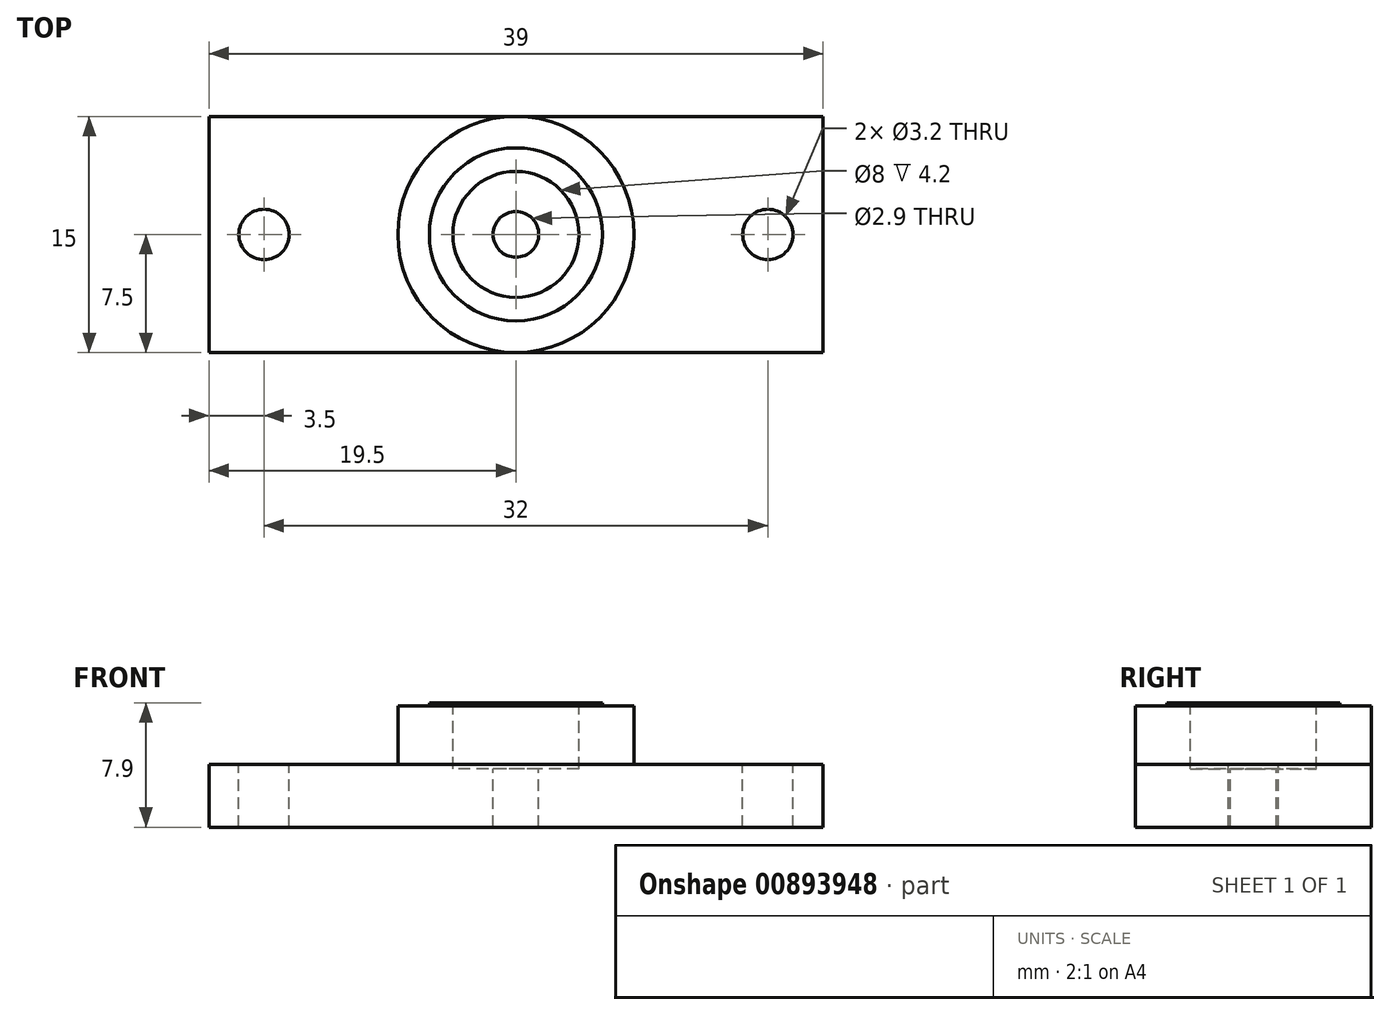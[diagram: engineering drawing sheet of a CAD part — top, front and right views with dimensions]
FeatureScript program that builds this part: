
annotation { "Feature Type Name" : "Feature", "Feature Type Description" : "" }
export const myFeature = defineFeature(function(context is Context, id is Id, definition is map)
    precondition{}
    {
        {
            var Q0;
            Q0=qCreatedBy(makeId("Top.planeOp"),FACE);
            var sketch = newSketch(context, id + "F0", { "sketchPlane" : qUnion([Q0])});
            skLineSegment(sketch, "E0.bottom", {"start": v(0, 0) * mm, "end": v(39, 0) * mm});
            skLineSegment(sketch, "E0.top", {"start": v(0, 15) * mm, "end": v(39, 15) * mm});
            skLineSegment(sketch, "E0.left", {"start": v(0, 0) * mm, "end": v(0, 15) * mm});
            skLineSegment(sketch, "E0.right", {"start": v(39, 0) * mm, "end": v(39, 15) * mm});
            skSolve(sketch);
        }
        {
            var Q0;
            Q0 = qSketchRegion(id + "F0", true);
            extrude(context, id + "F1", {"entities" : qUnion([Q0]), "depth" : 4 * mm, "offsetDistance" : 25 * mm});
        }
        {
            var Q0;
            Q0=makeQuery(id+"F1.opExtrude","CAP_FACE",FACE,{"disambiguationData":[OSD([sQuery(id+"F0.wireOp",EDGE,"E0.bottom"),sQuery(id+"F0.wireOp",EDGE,"E0.top"),sQuery(id+"F0.wireOp",EDGE,"E0.left"),sQuery(id+"F0.wireOp",EDGE,"E0.right")])],"isStart":false});
            var sketch = newSketch(context, id + "F2", { "sketchPlane" : qUnion([Q0])});
            skLineSegment(sketch, "E1", {"start": v(0, 7.5) * mm, "end": v(39, 7.5) * mm, "construction": true});
            skLineSegment(sketch, "E2", {"start": v(19.5, 15) * mm, "end": v(19.5, 0) * mm, "construction": true});
            skCircle(sketch, "E3", {"center": v(19.5, 7.5) * mm, "radius": 7.5 * mm});
            skSolve(sketch);
        }
        {
            var Q0;
            Q0 = qSketchRegion(id + "F2", true);
            extrude(context, id + "F3", {"entities" : qUnion([Q0]), "operationType" : NewBodyOperationType.ADD, "depth" : 3.9 * mm, "offsetDistance" : 25 * mm});
        }
        {
            var Q0;
            Q0=makeQuery(id+"F3.opExtrude","CAP_FACE",FACE,{"disambiguationData":[OSD([sQuery(id+"F2.wireOp",EDGE,"E3")])],"isStart":false});
            var sketch = newSketch(context, id + "F4", { "sketchPlane" : qUnion([Q0])});
            skCircle(sketch, "E4", {"center": v(19.5, 7.5) * mm, "radius": 4 * mm});
            skLineSegment(sketch, "E5", {"start": v(19.5, 15) * mm, "end": v(19.5, 0) * mm, "construction": true});
            skLineSegment(sketch, "E6", {"start": v(12, 7.5) * mm, "end": v(27, 7.5) * mm, "construction": true});
            skSolve(sketch);
        }
        {
            var Q0;
            Q0 = qSketchRegion(id + "F4", true);
            extrude(context, id + "F5", {"entities" : qUnion([Q0]), "operationType" : NewBodyOperationType.REMOVE, "depth" : -4.2 * mm, "offsetDistance" : 25 * mm});
        }
        {
            var Q0;
            Q0=makeQuery(id+"F1.opExtrude","CAP_FACE",FACE,{"disambiguationData":[OSD([sQuery(id+"F0.wireOp",EDGE,"E0.bottom"),sQuery(id+"F0.wireOp",EDGE,"E0.top"),sQuery(id+"F0.wireOp",EDGE,"E0.left"),sQuery(id+"F0.wireOp",EDGE,"E0.right")])],"isStart":false});
            var sketch = newSketch(context, id + "F6", { "sketchPlane" : qUnion([Q0])});
            skLineSegment(sketch, "E7", {"start": v(39, 7.5) * mm, "end": v(0, 7.5) * mm, "construction": true});
            skLineSegment(sketch, "E8", {"start": v(35.5, 15) * mm, "end": v(35.5, 0) * mm, "construction": true});
            skCircle(sketch, "E9.MirrorC", {"center": v(35.5, 7.5) * mm, "radius": 1.6 * mm});
            skCircle(sketch, "E10.MirrorC", {"center": v(3.5, 7.5) * mm, "radius": 1.6 * mm});
            skSolve(sketch);
        }
        {
            var Q0;
            Q0 = qSketchRegion(id + "F6", true);
            var Q1;
            Q1=makeQuery(id+"F6.imprint","IMPRINT",FACE,{"disambiguationData":[TD([[makeQuery(id+"F6.imprint","IMPRINT",EDGE,{"derivedFrom":sQuery(id+"F6.wireOp",EDGE,"maGDqfsK-tZUu-O8Bw-q2Sx-ifdf9yk7xXRb")}),1.0]])]});
            extrude(context, id + "F7", {"entities" : qUnion([Q0, Q1]), "operationType" : NewBodyOperationType.REMOVE, "oppositeDirection" : true, "depth" : 25 * mm, "offsetDistance" : 25 * mm});
        }
        {
            var Q0;
            Q0=makeQuery(id+"F5.boolean.opBoolean","COPY",FACE,{"derivedFrom":makeQuery(id+"F5.opExtrude","CAP_FACE",FACE,{"disambiguationData":[OSD([sQuery(id+"F4.wireOp",EDGE,"E4")])],"isStart":false})});
            var sketch = newSketch(context, id + "F8", { "sketchPlane" : qUnion([Q0])});
            skLineSegment(sketch, "E11", {"start": v(19.5, 11.5) * mm, "end": v(19.5, 3.5) * mm, "construction": true});
            skLineSegment(sketch, "E12", {"start": v(15.5, 7.5) * mm, "end": v(23.5, 7.5) * mm, "construction": true});
            skCircle(sketch, "E13", {"center": v(19.5, 7.5) * mm, "radius": 1.45 * mm});
            skSolve(sketch);
        }
        {
            var Q0;
            Q0 = qSketchRegion(id + "F8", true);
            extrude(context, id + "F9", {"entities" : qUnion([Q0]), "operationType" : NewBodyOperationType.REMOVE, "oppositeDirection" : true, "depth" : 25 * mm, "offsetDistance" : 25 * mm});
        }
        {
            var Q0;
            Q0=makeQuery(id+"F4.imprint","IMPRINT",FACE,{"disambiguationData":[TD([[makeQuery(id+"F4.imprint","IMPRINT",EDGE,{"derivedFrom":sQuery(id+"F4.wireOp",EDGE,"E4")}),-1.0]])]});
            var sketch = newSketch(context, id + "F10", { "sketchPlane" : qUnion([Q0])});
            skCircle(sketch, "E14", {"center": v(19.5, 7.5) * mm, "radius": 5.5 * mm});
            skSolve(sketch);
        }
        {
            var Q0;
            Q0=makeQuery(id+"F10.imprint","IMPRINT",FACE,{"disambiguationData":[TD([[makeQuery(id+"F10.imprint","IMPRINT",EDGE,{"derivedFrom":sQuery(id+"F10.wireOp",EDGE,"E14")}),-1.0]])]});
            extrude(context, id + "F11", {"entities" : qUnion([Q0]), "operationType" : NewBodyOperationType.REMOVE, "oppositeDirection" : true, "depth" : 0.2 * mm, "offsetDistance" : 25 * mm});
        }
    });
